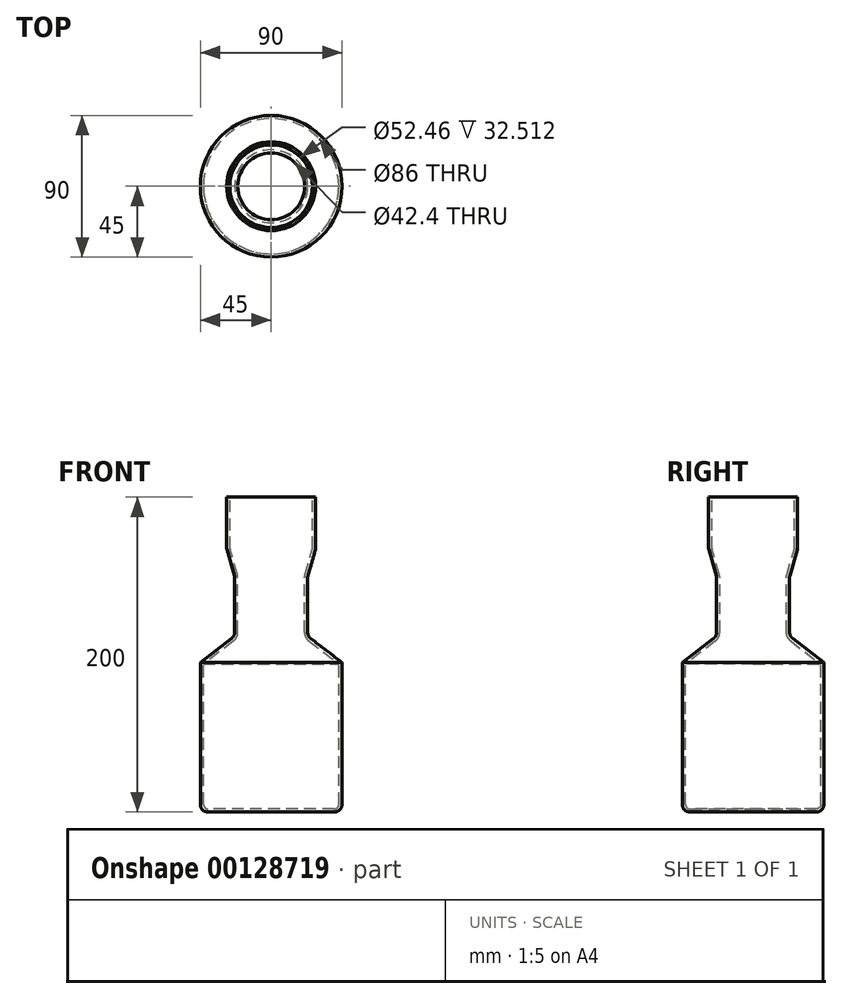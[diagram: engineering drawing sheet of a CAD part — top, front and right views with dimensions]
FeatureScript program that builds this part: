
annotation { "Feature Type Name" : "Feature", "Feature Type Description" : "" }
export const myFeature = defineFeature(function(context is Context, id is Id, definition is map)
    precondition{}
    {
        {
            var Q0;
            Q0=qCreatedBy(makeId("Front.planeOp"),FACE);
            var sketch = newSketch(context, id + "F0", { "sketchPlane" : qUnion([Q0])});
            skLineSegment(sketch, "E0", {"start": v(0, 0) * mm, "end": v(40, 0) * mm});
            skLineSegment(sketch, "E1", {"start": v(45, 5) * mm, "end": v(45, 95.03) * mm});
            skLineSegment(sketch, "E2", {"start": v(45, 95.03) * mm, "end": v(25.16, 110.24) * mm});
            skLineSegment(sketch, "E3", {"start": v(23.2, 114.2) * mm, "end": v(23.2, 149.2) * mm});
            skLineSegment(sketch, "E4", {"start": v(23.32, 150.04) * mm, "end": v(28.11, 166.66) * mm});
            skLineSegment(sketch, "E5", {"start": v(28.23, 167.49) * mm, "end": v(28.23, 200) * mm});
            skLineSegment(sketch, "E6", {"start": v(28.23, 200) * mm, "end": v(0, 200) * mm});
            skLineSegment(sketch, "E7", {"start": v(0, 200) * mm, "end": v(0, 0) * mm});
            skPoint(sketch, "E8.visualSharp", {"position": v(23.2, 149.63) * mm});
            skArc(sketch, "E8.filletArc", {"start": v(23.32, 150.04) * mm, "mid": v(23.23, 149.63) * mm, "end": v(23.2, 149.2) * mm});
            skPoint(sketch, "E9.visualSharp", {"position": v(28.23, 167.06) * mm});
            skArc(sketch, "E9.filletArc", {"start": v(28.11, 166.66) * mm, "mid": v(28.2, 167.07) * mm, "end": v(28.23, 167.49) * mm});
            skPoint(sketch, "E10.visualSharp", {"position": v(23.2, 111.74) * mm});
            skArc(sketch, "E10.filletArc", {"start": v(23.2, 114.2) * mm, "mid": v(23.72, 112) * mm, "end": v(25.16, 110.24) * mm});
            skPoint(sketch, "E11.visualSharp", {"position": v(45, 0) * mm});
            skArc(sketch, "E11.filletArc", {"start": v(40, 0) * mm, "mid": v(43.54, 1.46) * mm, "end": v(45, 5) * mm});
            skSolve(sketch);
        }
        {
            var Q0;
            Q0 = qSketchRegion(id + "F0", true);
            var Q1;
            Q1=sQuery(id+"F0.wireOp",EDGE,"E7");
            revolve(context, id + "F1", {"entities" : qUnion([Q0]), "axis" : qUnion([Q1]), "revolveType" : RevolveType.FULL});
        }
        {
            var Q0;
            Q0=makeQuery(id+"F1.opRevolve","SWEPT_FACE",FACE,{"disambiguationData":[OSD([sQuery(id+"F0.wireOp",EDGE,"E6")])]});
            shell(context, id + "F2", {"entities" : qUnion([Q0]), "thickness" : 2 * mm});
        }
    });
